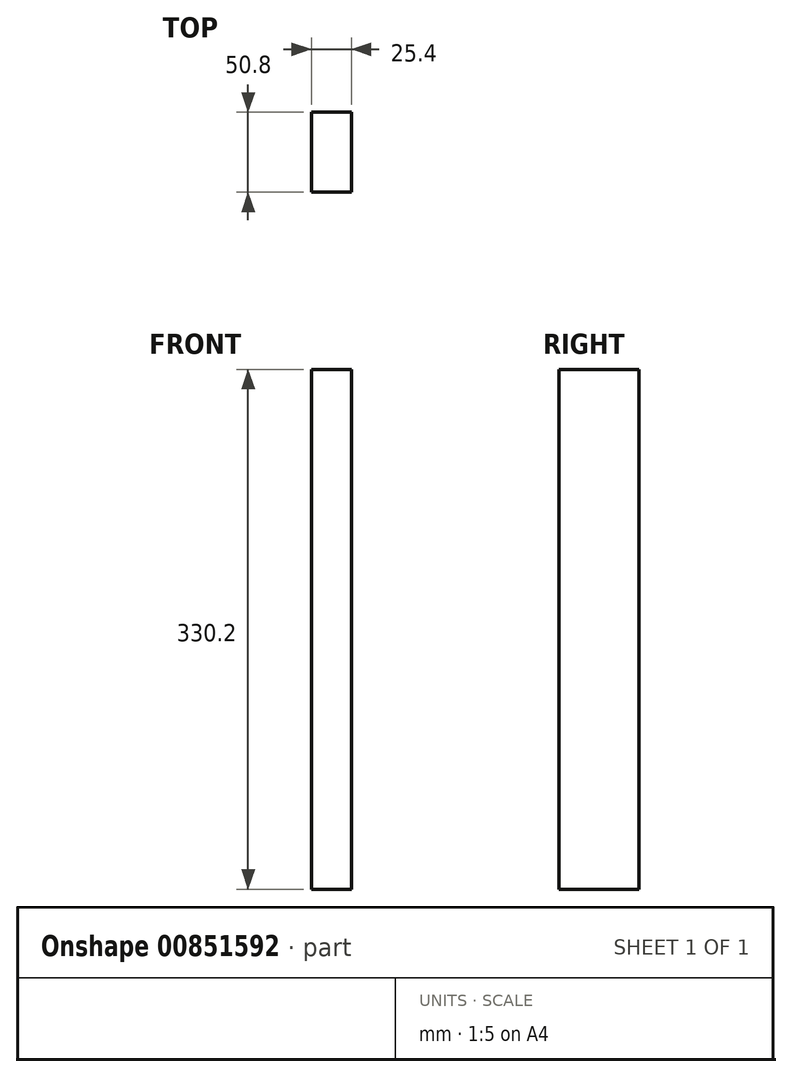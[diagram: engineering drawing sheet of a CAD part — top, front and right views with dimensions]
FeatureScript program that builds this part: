
annotation { "Feature Type Name" : "Feature", "Feature Type Description" : "" }
export const myFeature = defineFeature(function(context is Context, id is Id, definition is map)
    precondition{}
    {
        {
            var Q0;
            Q0=qCreatedBy(makeId("Front.planeOp"),FACE);
            var sketch = newSketch(context, id + "F0", { "sketchPlane" : qUnion([Q0])});
            skLineSegment(sketch, "E0.bottom", {"start": v(-73.9, 182.76) * mm, "end": v(-48.5, 182.76) * mm});
            skLineSegment(sketch, "E0.top", {"start": v(-73.9, -147.44) * mm, "end": v(-48.5, -147.44) * mm});
            skLineSegment(sketch, "E0.left", {"start": v(-73.9, 182.76) * mm, "end": v(-73.9, -147.44) * mm});
            skLineSegment(sketch, "E0.right", {"start": v(-48.5, 182.76) * mm, "end": v(-48.5, -147.44) * mm});
            skSolve(sketch);
        }
        {
            var Q0;
            Q0 = qSketchRegion(id + "F0", true);
            extrude(context, id + "F1", {"entities" : qUnion([Q0]), "depth" : 50.8 * mm, "offsetDistance" : 25.4 * mm});
        }
    });
